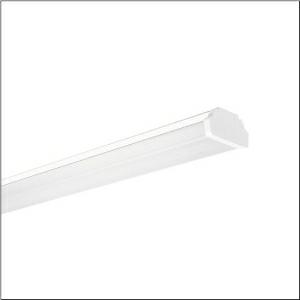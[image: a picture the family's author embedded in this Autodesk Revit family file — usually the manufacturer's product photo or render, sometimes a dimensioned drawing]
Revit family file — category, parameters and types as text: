
# Revit family: dus_r__31_mo_53bd812c1v6075_124e
name_source: partatom
category: Lighting Fixtures
units: mm (PartAtom-declared; Revit-internal decimal feet)

## family parameters
Cut with Voids When Loaded = No
Host = Face
Light Source = No
Part Type = Normal
Room Calculation Point = No
Round Connector Dimension = Use Diameter
Shared = No

## types (1)
- --- (1 x LED, 7640 lm, 48.9 W, 6500K)
    Apparent Load = 49 VA
    CIE Flux Codes = 47 80 95 92 100
    Color Rendering = 80
    Color Temperature = 6500K
    Default Elevation = 1800 mm
    Description = DUS® 31 MOluminaire insert, length: 1.535mm, width: 81mm, height: 90mm, LED rated luminous flux: 7.640lm, light colour: 865, control gear: ON/OFF Multilumen, CLOi, control gear: ECG Multilumen, with plug, 3-pole, with phase selection, mains connection: 220..240V, AC, 50/60Hz, primary optical cover: cover, of PMMA, light emission: direct distribution, primary light characteristic: symmetric, protection rating (complete): IP20, protection rating (LED compartment): IP50, insulation class (complete): insulation class I (protective earthing), certification: CE, ENEC, VDE, UKCA, permissible ambient temperature for indoor applications: -35..+30°C, corresponds to IFS (International Featured Standards) requirements for safety and quality in the food industry, reducing of maximum allowable ambient temperature of 5°C with ceiling mounting, packaging unit: 1 piece
    Height = 95 mm
    Lamp = 1 x LED
    Lamp Light Flux = 7640 lm
    Lamp Power = 48.9 W
    Lamp count = 1
    Length = 1535 mm
    Luminous efficacy = 156 lm/W
    Manufacturer = Siteco
    ModVariant = No
    Model = 53BD812C1V6075
    Mounting Place = Ceiling
    Mounting Type = Pendant
    Number of Poles = 1
    OnlyDefault = Yes
    Power Factor = 1
    Product Name = DUS® 31 MO
    Product group = luminaire insert
    ProductGroupID = 902
    Protection Class = Protection class I
    Protection Degree = IP 20
    RLX_Detail_Level = 1
    RlxData = <blob elided: 39589 chars, md5=7604fb54>
    Socket = socket
    Standby Power = 0 W
    System Light Flux = 7640 lm
    System Power = 49 W
    Type Comments = factory setting: luminous flux: 100 % | (A | C | E) | 107 mA
    Type Image = l_1003451.jpg
    URL = http://relux.com
    VarID = @adj_131317
    Voltage = 0 V
    Weight = 0.00 kg
    Width = 81 mm

## geometry (parser evidence)
native form markers: Blend x4, Sweep x12
no freeform markers — native parametric forms only
